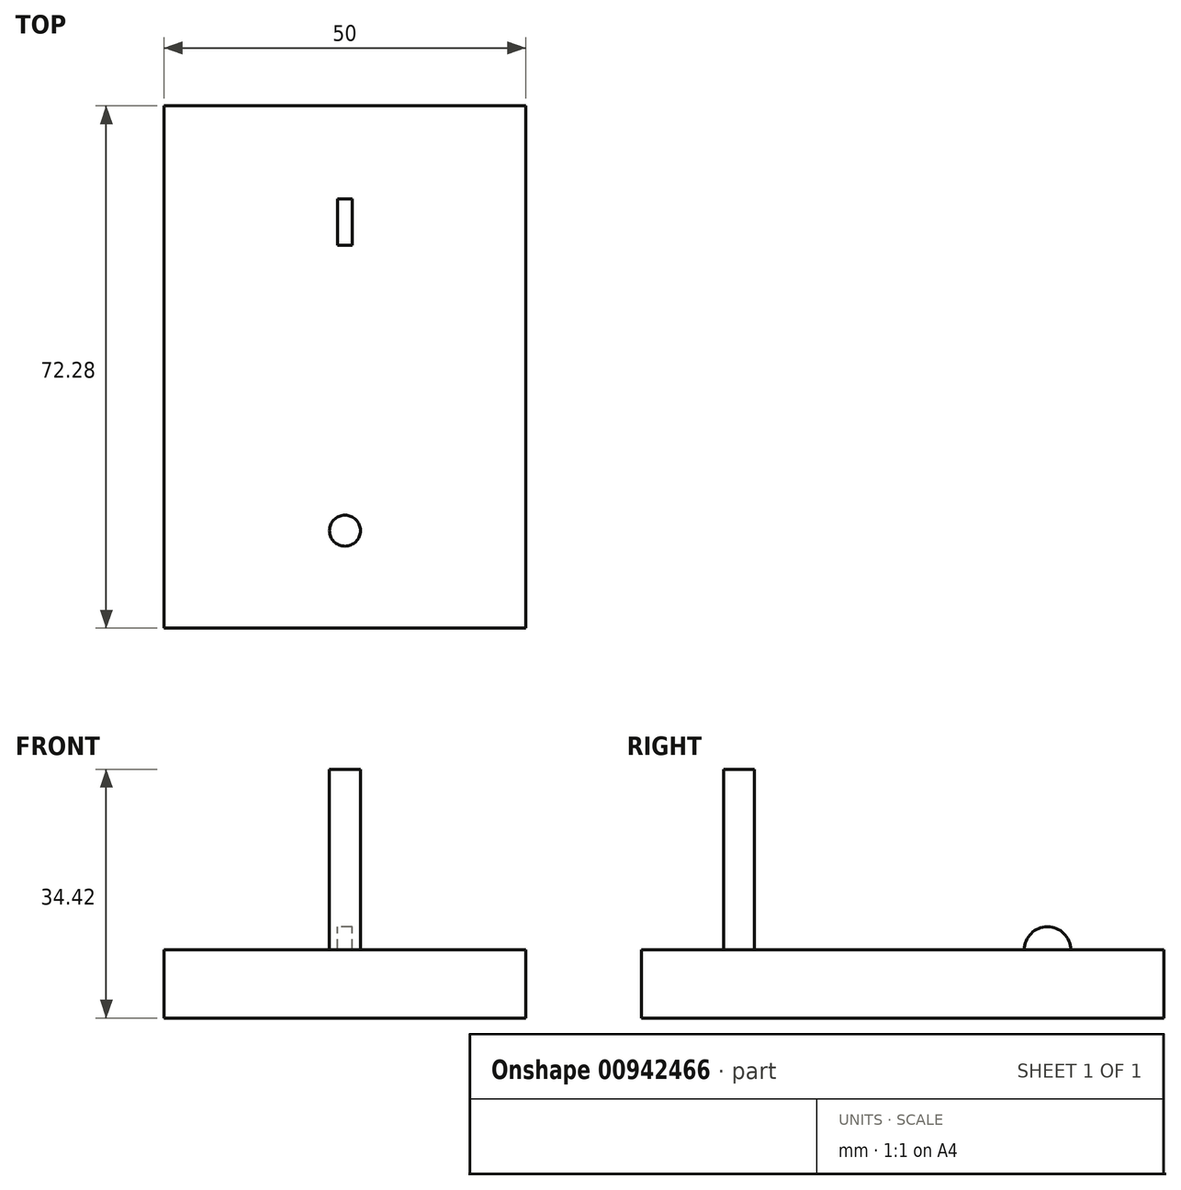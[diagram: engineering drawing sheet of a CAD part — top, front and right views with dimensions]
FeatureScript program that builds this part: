
annotation { "Feature Type Name" : "Feature", "Feature Type Description" : "" }
export const myFeature = defineFeature(function(context is Context, id is Id, definition is map)
    precondition{}
    {
        {
            var Q0;
            Q0=qCreatedBy(makeId("Right.planeOp"),FACE);
            var sketch = newSketch(context, id + "F0", { "sketchPlane" : qUnion([Q0])});
            skLineSegment(sketch, "E0.bottom", {"start": v(36.14, 4.71) * mm, "end": v(-36.14, 4.71) * mm});
            skLineSegment(sketch, "E0.top", {"start": v(36.14, -4.71) * mm, "end": v(-36.14, -4.71) * mm});
            skLineSegment(sketch, "E0.left", {"start": v(36.14, 4.71) * mm, "end": v(36.14, -4.71) * mm});
            skLineSegment(sketch, "E0.right", {"start": v(-36.14, 4.71) * mm, "end": v(-36.14, -4.71) * mm});
            skPoint(sketch, "E0.middle", {"position": v(0, 0) * mm});
            skSolve(sketch);
        }
        {
            var Q0;
            Q0=makeQuery(id+"F0.imprint","IMPRINT",FACE,{"disambiguationData":[TD([[makeQuery(id+"F0.imprint","IMPRINT",EDGE,{"derivedFrom":sQuery(id+"F0.wireOp",EDGE,"E0.bottom")}),1.0]])]});
            extrude(context, id + "F1", {"entities" : qUnion([Q0]), "endBound" : BoundingType.SYMMETRIC, "depth" : 50 * mm, "offsetDistance" : 25 * mm});
        }
        {
            var Q0;
            Q0=makeQuery(id+"F1.opExtrude","SWEPT_FACE",FACE,{"disambiguationData":[OSD([sQuery(id+"F0.wireOp",EDGE,"E0.bottom")])]});
            var sketch = newSketch(context, id + "F2", { "sketchPlane" : qUnion([Q0])});
            skCircle(sketch, "E1", {"center": v(0, -22.63) * mm, "radius": 2.14 * mm});
            skSolve(sketch);
        }
        {
            var Q0;
            Q0=makeQuery(id+"F2.imprint","IMPRINT",FACE,{"disambiguationData":[TD([[makeQuery(id+"F2.imprint","IMPRINT",EDGE,{"derivedFrom":sQuery(id+"F2.wireOp",EDGE,"E1")}),1.0]])]});
            extrude(context, id + "F3", {"entities" : qUnion([Q0]), "operationType" : NewBodyOperationType.ADD, "depth" : 25 * mm, "offsetDistance" : 25 * mm});
        }
        {
            var Q0;
            Q0=qCreatedBy(makeId("Right.planeOp"),FACE);
            var sketch = newSketch(context, id + "F4", { "sketchPlane" : qUnion([Q0])});
            skLineSegment(sketch, "E2.0", {"start": v(36.14, 4.71) * mm, "end": v(-36.14, 4.71) * mm, "construction": true});
            skCircle(sketch, "E3", {"center": v(20.03, 4.71) * mm, "radius": 3.2 * mm});
            skSolve(sketch);
        }
        {
            var Q0;
            Q0=makeQuery(id+"F4.imprint","IMPRINT",FACE,{"disambiguationData":[TD([[makeQuery(id+"F4.imprint","IMPRINT",EDGE,{"derivedFrom":sQuery(id+"F4.wireOp",EDGE,"E3")}),1.0]])]});
            extrude(context, id + "F5", {"entities" : qUnion([Q0]), "operationType" : NewBodyOperationType.ADD, "endBound" : BoundingType.SYMMETRIC, "depth" : 2 * mm, "offsetDistance" : 25 * mm});
        }
    });
